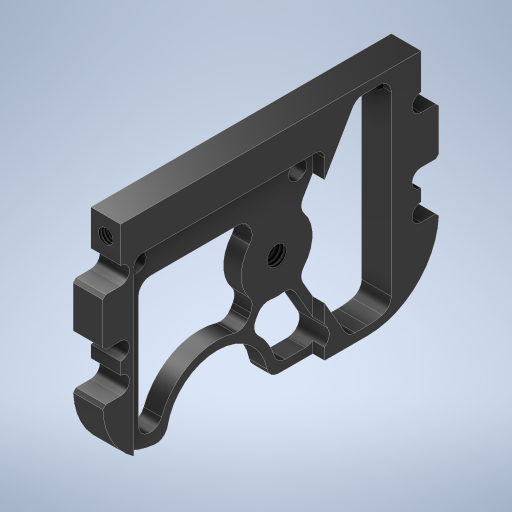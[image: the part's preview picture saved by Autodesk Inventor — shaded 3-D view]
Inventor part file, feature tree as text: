
AUTODESK INVENTOR PART (.ipt)
format: ipt  version: 2024.2 (Build 282272000, 272)  size: 467,968 bytes
history: native  units: mm
features: extrude x2, fillet x2, hole x2, other x1, chamfer x1, sketch x1
ambient origin geometry x8: Origin, YZ Plane, XZ Plane, XY Plane, X Axis, Y Axis, Z Axis, Center Point
bodies: Solid1 (feature_tree)
feature tree (9):
  other  "UpperArmSideFrameBasis.ipt"
  extrude  "Extrusion1"  Depth=2.0mm
  extrude  "Extrusion2"  TaperAngle=0.0deg  [1 undecoded]
  fillet  "Fillet1"  Radius=2.0mm
  fillet  "Fillet2"  Radius=2.0mm
  chamfer  "Chamfer1"  [1 undecoded]
  hole  "Phi3.1"  [1 undecoded]
  hole  "Side-M3"  [1 undecoded]
  sketch  "Sketch1"  dims[d0=10.0mm d1=5.0mm d2=0.0mm d17=0.5mm d18=2.0mm d19=45.0deg d20=3.1mm d21=6.0mm d22=4.0mm d23=2.0mm d24=90.0deg d25=8.0mm d26=0.0mm d27=3.242mm d28=8.0mm d29=4.0mm d30=2.0mm d31=90.0deg d32=8.0mm d33=0.0mm d34=2.0mm d35=0.0mm d41=2.459mm d42=6.0mm d43=4.0mm d44=2.0mm d45=90.0deg d46=6.0mm d47=0.0mm d55=1.5mm d56=2.0mm d36=0.5mm d37=0.872665mm]
note: 4 required parameter values undecoded (feature->parameter linkage not recoverable at this tier; creation-order binding heuristic only, values carry confidence <= 0.55)
